# Revit family: Water-Filter_Whole-House
name_source: partatom
category: Plumbing Fixtures
units: mm (PartAtom-declared; Revit-internal decimal feet)

## family parameters
Always vertical = Yes
Classification Number = 23.65.50.11.11.11
Cut with Voids When Loaded = No
Enable Cutting in Views = No
Maintain Annotation Orientation = No
Part Type = Normal
Room Calculation Point = No
Round Connector Dimension = Use Diameter
Shared = No
Work Plane-Based = Yes

## types (1)
- Water-Filter_Whole-House
    Amperage = 3
    Assembly Code = D2020300
    Backwash (GPM) = 2
    Body Material = ARCAT - Metal - Aluminum, Painted - Light Blue
    Brine Connection = 3/8" NPT
    CW Connection = No
    Construction Details = http://www.arcat.com
    Default Elevation = 4' - 0"
    Description = Residential Water Filtration System
    Expected Lifespan (Years) = 15
    Fitting Material = ARCAT - Metal - Brass
    Flow Range = 9 - 15 GPM
    Green Building-LEED = http://www.arcat.com
    Inlet Connection = Plumbing-Connector : Thread-Thread -B-C 1
    Keynote = 15470
    Maintenance Schedule (Months) = 1
    Manufacturer = Generic
    Manufacturer Fax = (203) 939-2444
    Manufacturer Website = http://www.arcat.com
    Max Water Temp - F = 200
    Media Type = High capacity fine mesh cation resin
    Model = Generic
    Outlet Connection = Plumbing-Connector : Thread-Thread -B-C 1
    Product Data = http://www.arcat.com
    Product Properties = http://www.arcat.com
    Regeneration = 15 minutes/ 15 gal. Countercurrent
    Size - Grains = 3000
    Specification = http://www.arcat.com
    Tank Capacity (Lbs) = 250
    Voltage = 110
    Warranty Duration (Years) = 10
    Water Heater Size = 120
    Wattage = 15
    Working Pressure = 15-125 PSI

## geometry (parser evidence)
native form markers: Sweep x8
no freeform markers — native parametric forms only
